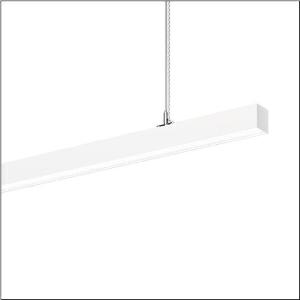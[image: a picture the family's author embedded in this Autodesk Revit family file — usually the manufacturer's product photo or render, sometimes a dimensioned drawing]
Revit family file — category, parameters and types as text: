
# Revit family: silica_r__21_51mx33db49wb_5808
name_source: partatom
category: Lighting Fixtures
units: mm (PartAtom-declared; Revit-internal decimal feet)

## family parameters
Cut with Voids When Loaded = No
Host = Face
Light Source = No
Part Type = Normal
Room Calculation Point = No
Round Connector Dimension = Use Diameter
Shared = No

## types (1)
- --- (1 x LED, 7390 lm, 48.3 W, 4000K)
    Apparent Load = 48 VA
    CIE Flux Codes = 78 96 99 55 100
    Color Rendering = 80
    Color Temperature = 4000K
    Default Elevation = 1800 mm
    Description = Silica® 21, office luminaire, primary optical cover: prismatic diffuser, of PMMA, CAT 2 (L<= 3000cd/m²), light emission: direct/indirect distribution, primary light characteristic: symmetric, installation type: suspended mounting, LED, rated luminous flux: 7.390lm, luminous efficacy: 153lm/W, light colour: 840, colour temperature: 4000K, with terminal, 3+2-pole, max. 2.5mm², mains connection: 220..240V, AC, 50/60Hz, rated input power: 48.3W, luminaire housing, of aluminium, traffic white (RAL 9016), length: 1.504mm, width: 53mm, height: 53mm, protection rating (complete): IP20, insulation class (complete): insulation class I (protective earthing), certification: CE, permissible operating ambient temperature: 0..+35°C, standard: EN 50419, packaging unit: 1 piece
    Height = 53 mm
    Lamp = 1 x LED
    Lamp Light Flux = 7390 lm
    Lamp Power = 48.3 W
    Lamp count = 1
    Length = 1504 mm
    Luminous efficacy = 153 lm/W
    Manufacturer = Siteco
    ModVariant = No
    Model = 51MX33DB49WB
    Mounting Place = Ceiling
    Mounting Type = Pendant
    Number of Poles = 1
    OnlyDefault = Yes
    Power Factor = 1
    Product Name = Silica® 21
    Product group = office luminaire | ceiling pendant
    ProductGroupID = 902
    Protection Class = Protection class I
    Protection Degree = IP 20
    RLX_Detail_Level = 1
    RLX_Emergency_Light_Flux = 0 lm
    RLX_Emergency_Type = 0
    RLX_Emergency_Type_DB = No
    RlxData = <blob elided: 21417 chars, md5=afcfdbf7>
    Socket = socket
    Standby Power = 0 W
    System Light Flux = 7390 lm
    System Power = 48 W
    Type Comments = factory setting: luminous flux: 100 % | dim-lin: 254 | 323 mA
    Type Image = l_1313629.jpg
    URL = http://relux.com
    VarID = @adj_066727
    Voltage = 0 V
    Weight = 0.00 kg
    Width = 53 mm

## geometry (parser evidence)
native form markers: Blend x4, Sweep x13
no freeform markers — native parametric forms only
